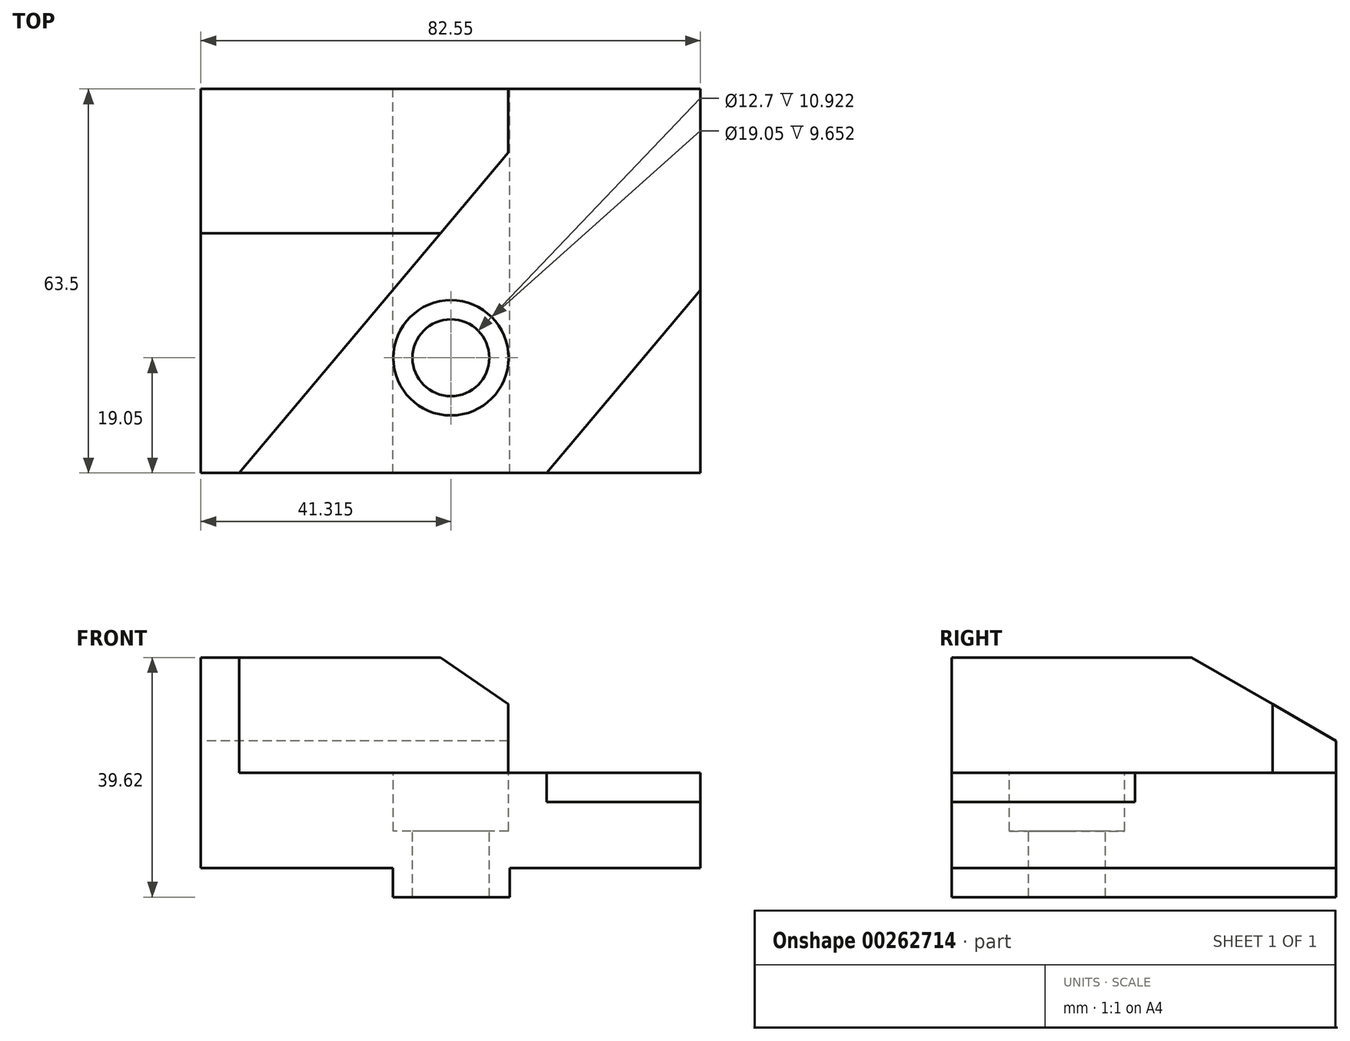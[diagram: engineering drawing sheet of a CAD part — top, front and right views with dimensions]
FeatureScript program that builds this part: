
annotation { "Feature Type Name" : "Feature", "Feature Type Description" : "" }
export const myFeature = defineFeature(function(context is Context, id is Id, definition is map)
    precondition{}
    {
        {
            var Q0;
            Q0=qCreatedBy(makeId("Front.planeOp"),FACE);
            var sketch = newSketch(context, id + "F0", { "sketchPlane" : qUnion([Q0])});
            skLineSegment(sketch, "E0", {"start": v(-2.84, -8.01) * mm, "end": v(-22.14, -8.01) * mm});
            skLineSegment(sketch, "E1", {"start": v(-22.14, -8.01) * mm, "end": v(-22.14, -3.19) * mm});
            skLineSegment(sketch, "E2", {"start": v(-22.14, -3.19) * mm, "end": v(-53.89, -3.19) * mm});
            skLineSegment(sketch, "E3", {"start": v(-53.89, -3.19) * mm, "end": v(-53.89, 31.61) * mm});
            skLineSegment(sketch, "E4", {"start": v(-53.89, 31.61) * mm, "end": v(-3.09, 31.61) * mm});
            skLineSegment(sketch, "E5", {"start": v(-3.09, 31.61) * mm, "end": v(-3.09, 12.56) * mm});
            skLineSegment(sketch, "E6", {"start": v(-3.09, 12.56) * mm, "end": v(28.66, 12.56) * mm});
            skLineSegment(sketch, "E7", {"start": v(28.66, 12.56) * mm, "end": v(28.66, -3.19) * mm});
            skLineSegment(sketch, "E8", {"start": v(28.66, -3.19) * mm, "end": v(-2.84, -3.19) * mm});
            skLineSegment(sketch, "E9", {"start": v(-2.84, -3.19) * mm, "end": v(-2.84, -8.01) * mm});
            skPoint(sketch, "E10", {"position": v(-12.49, -8.01) * mm});
            skSolve(sketch);
        }
        {
            var Q0;
            Q0=makeQuery(id+"F0.imprint","IMPRINT",FACE,{"disambiguationData":[TD([[makeQuery(id+"F0.imprint","IMPRINT",EDGE,{"derivedFrom":sQuery(id+"F0.wireOp",EDGE,"E0")}),-1.0]])]});
            extrude(context, id + "F1", {"entities" : qUnion([Q0]), "endBound" : BoundingType.SYMMETRIC, "depth" : 63.5 * mm});
        }
        {
            var Q0;
            Q0=makeQuery(id+"F1.opExtrude","SWEPT_FACE",FACE,{"disambiguationData":[OSD([sQuery(id+"F0.wireOp",EDGE,"E4")])]});
            var sketch = newSketch(context, id + "F2", { "sketchPlane" : qUnion([Q0])});
            skLineSegment(sketch, "E11", {"start": v(-53.89, -31.75) * mm, "end": v(-47.54, -31.75) * mm});
            skLineSegment(sketch, "E12", {"start": v(-47.54, -31.75) * mm, "end": v(-3.09, 21.22) * mm});
            skSolve(sketch);
        }
        {
            var Q0;
            {var subQ0=sQuery(id+"F2.wireOp",EDGE,"E12");Q0=makeQuery(id+"F2.imprint","IMPRINT",FACE,{"disambiguationData":[TD([[makeQuery(id+"F2.imprint","IMPRINT",EDGE,{"derivedFrom":subQ0}),-1.0]])]});}
            extrude(context, id + "F3", {"entities" : qUnion([Q0]), "operationType" : NewBodyOperationType.REMOVE, "oppositeDirection" : true, "depth" : 19.05 * mm});
        }
        {
            var Q0;
            Q0=makeQuery(id+"F3.boolean.opBoolean","MERGE",FACE,{"derivedFrom":[makeQuery(id+"F1.opExtrude","SWEPT_FACE",FACE,{"disambiguationData":[OSD([sQuery(id+"F0.wireOp",EDGE,"E6")])]}),makeQuery(id+"F3.opExtrude","CAP_FACE",FACE,{"disambiguationData":[OSD([sQuery(id+"F0.wireOp",EDGE,"E4"),sQuery(id+"F0.wireOp",EDGE,"E5"),sQuery(id+"F2.wireOp",EDGE,"E12")])],"isStart":false})]});
            var sketch = newSketch(context, id + "F4", { "sketchPlane" : qUnion([Q0])});
            skLineSegment(sketch, "E13", {"start": v(28.66, -31.75) * mm, "end": v(3.26, -31.75) * mm});
            skLineSegment(sketch, "E14", {"start": v(3.26, -31.75) * mm, "end": v(28.66, -1.48) * mm});
            skSolve(sketch);
        }
        {
            var Q0;
            {var subQ0=sQuery(id+"F4.wireOp",EDGE,"E13");Q0=makeQuery(id+"F4.imprint","IMPRINT",FACE,{"disambiguationData":[TD([[makeQuery(id+"F4.imprint","IMPRINT",EDGE,{"derivedFrom":subQ0}),1.0]])]});}
            extrude(context, id + "F5", {"entities" : qUnion([Q0]), "operationType" : NewBodyOperationType.REMOVE, "oppositeDirection" : true, "depth" : 4.83 * mm});
        }
        {
            var Q0;
            Q0=makeQuery(id+"F1.opExtrude","SWEPT_FACE",FACE,{"disambiguationData":[OSD([sQuery(id+"F0.wireOp",EDGE,"E3")])]});
            var sketch = newSketch(context, id + "F6", { "sketchPlane" : qUnion([Q0])});
            skLineSegment(sketch, "E15", {"start": v(-7.87, 31.61) * mm, "end": v(-31.75, 17.83) * mm});
            skLineSegment(sketch, "E16", {"start": v(-31.75, 17.83) * mm, "end": v(-31.75, 31.61) * mm});
            skLineSegment(sketch, "E17", {"start": v(-31.75, 31.61) * mm, "end": v(-7.87, 31.61) * mm});
            skSolve(sketch);
        }
        {
            var Q0;
            Q0=makeQuery(id+"F6.imprint","IMPRINT",FACE,{"disambiguationData":[TD([[makeQuery(id+"F6.imprint","IMPRINT",EDGE,{"derivedFrom":sQuery(id+"F6.wireOp",EDGE,"E15")}),-1.0]])]});
            extrude(context, id + "F7", {"entities" : qUnion([Q0]), "operationType" : NewBodyOperationType.REMOVE, "oppositeDirection" : true, "depth" : 52.43 * mm});
        }
        {
            var Q0;
            Q0=makeQuery(id+"F3.boolean.opBoolean","MERGE",FACE,{"derivedFrom":[makeQuery(id+"F1.opExtrude","SWEPT_FACE",FACE,{"disambiguationData":[OSD([sQuery(id+"F0.wireOp",EDGE,"E6")])]}),makeQuery(id+"F3.opExtrude","CAP_FACE",FACE,{"disambiguationData":[OSD([sQuery(id+"F0.wireOp",EDGE,"E4"),sQuery(id+"F0.wireOp",EDGE,"E5"),sQuery(id+"F2.wireOp",EDGE,"E12")])],"isStart":false})]});
            var sketch = newSketch(context, id + "F8", { "sketchPlane" : qUnion([Q0])});
            skLineSegment(sketch, "E18", {"start": v(-12.57, -31.75) * mm, "end": v(-12.57, -12.7) * mm});
            skSolve(sketch);
        }
        {
            var Q0;
            Q0=sQuery(id+"F8.wireOp",VERTEX,"E18.end");
            var Q1;
            Q1=makeQuery(id+"F1.opExtrude","SWEPT_BODY",BODY,{"disambiguationData":[OSD([sQuery(id+"F0.wireOp",EDGE,"E0"),sQuery(id+"F0.wireOp",EDGE,"E1"),sQuery(id+"F0.wireOp",EDGE,"E2"),sQuery(id+"F0.wireOp",EDGE,"E3"),sQuery(id+"F0.wireOp",EDGE,"E4"),sQuery(id+"F0.wireOp",EDGE,"E5"),sQuery(id+"F0.wireOp",EDGE,"E6"),sQuery(id+"F0.wireOp",EDGE,"E7"),sQuery(id+"F0.wireOp",EDGE,"E8"),sQuery(id+"F0.wireOp",EDGE,"E9")])]});
            hole(context, id + "F9", {"style" : HoleStyle.C_BORE, "endStyle" : HoleEndStyle.THROUGH, "holeDiameter" : 12.7 * mm, "cBoreDiameter" : 19.05 * mm, "cBoreDepth" : 9.65 * mm, "tappedDepth" : 12.7 * mm, "tapClearance" : 3, "locations" : qUnion([Q0]), "scope" : qUnion([Q1])});
        }
    });
